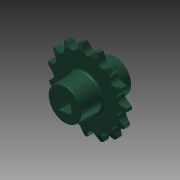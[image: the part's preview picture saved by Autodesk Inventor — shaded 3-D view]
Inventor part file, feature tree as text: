
AUTODESK INVENTOR PART (.ipt)
format: ipt  version: 2013 (Build 170138000, 138)  size: 1,111,040 bytes
history: native  units: mm (DEFAULTED — no unit token found)
features: imported_body x1, sketch x1, other x1, extrude x1
ambient origin geometry x8: Origin, YZ Plane, XZ Plane, XY Plane, X Axis, Y Axis, Z Axis, Center Point
bodies: Solid1 (feature_tree)
feature tree (4):
  imported_body  "Base1"
  sketch  "Sketch1"  dims[d1=2.2606mm d5=25.4mm d6=0.0mm d7=0.0mm d8=0.0mm]
  other  "Srf1"
  extrude  "ExtrusionSrf1"  Depth=25.4mm TaperAngle=0.0deg
